# Revit family: UB90.xxx.T_RVT15
name_source: partatom
category: Möbelsysteme
revit_build: Autodesk Revit 2015 (Build: 20160512_1515(x64)
units: mm (PartAtom-declared; Revit-internal decimal feet)

## types (12) — shared parameters
1100/600 2T 2nd lvl = Nein
Beschreibung = GS-tested safety storage underbench cabinets for unrestricted storage of flammable hazardous materials in work areas in accordance with EN 14470-1 and TRGS 510 with a fire resistance of 90 (Type 90)
Cabinet & door colour = RAL 7035 Light grey
Cabinet height = 600 mm
Diff. pressure (Air change 10 times) = 1.0 Pa
Hersteller = asecos GmbH
Price information = Price from fall 2017
Price information 2 = Prices are ex works and without taxes and shipping
Product video = https://www.youtube.com
URL = https://www.asecos.com
ex. air pos. 2 = 130 mm  [stored 0.426509 ft]

## per-type parameters (varying)
- UB90.060.089.2T: 1100/500 2T 2nd lvl=Nein; 1100/500 2T perf. insert=Nein; 1100/600 2T perf. insert=Nein; 590/500 2nd lvl=Nein; 590/500 perf. insert=Nein; 590/600 2nd lvl=Nein; 590/600 perf. insert=Nein; 890/500 2T 2nd lvl=Nein; 890/500 2T perf. insert=Nein; 890/600 2T 2nd lvl=Nein; 890/600 2T perf. insert=Ja; Air change 10 times=0.6 L/s; Bestellnummer DACH=30464-001-30466; Cabinet depth=574 mm  [stored 1.8832 ft]; Cabinet width=893 mm  [stored 2.92979 ft]; Distributed load=3.07 kN/m²; Door width=416 mm; Door width RS=416 mm; Double door=Ja; Handle position=49 mm  [stored 0.160761 ft]; Kosten=1771.5 $; Modell=UB90.060.089.2T, light grey, bottom collecting sump with perforated insert; Order No. Global=30464-001-30466; Single door=Nein; Sticker HI=Nein; Sticker LO=Ja; Typenbild=30464-001.jpg; ex. air pos. 1=301 mm  [stored 0.987533 ft]
- UB90.060.059.050.T: 1100/500 2T 2nd lvl=Nein; 1100/500 2T perf. insert=Nein; 1100/600 2T perf. insert=Nein; 590/500 2nd lvl=Nein; 590/500 perf. insert=Ja; 590/600 2nd lvl=Nein; 590/600 perf. insert=Nein; 890/500 2T 2nd lvl=Nein; 890/500 2T perf. insert=Nein; 890/600 2T 2nd lvl=Nein; 890/600 2T perf. insert=Nein; Air change 10 times=0.3 L/s; Bestellnummer DACH=30483-001-30490; Cabinet depth=503 mm; Cabinet width=593 mm  [stored 1.94554 ft]; Distributed load=4.51 kN/m²; Door width=539 mm; Door width RS=495 mm; Double door=Nein; Handle position=73 mm; Kosten=1318 $; Modell=UB90.060.059.050.T, light grey, bottom collecting sump with perforated insert; Order No. Global=30483-001-30490; Single door=Ja; Sticker HI=Ja; Sticker LO=Nein; Typenbild=30483-001.jpg; ex. air pos. 1=182 mm
- UB90.060.059.T: 1100/500 2T 2nd lvl=Nein; 1100/500 2T perf. insert=Nein; 1100/600 2T perf. insert=Nein; 590/500 2nd lvl=Nein; 590/500 perf. insert=Nein; 590/600 2nd lvl=Nein; 590/600 perf. insert=Ja; 890/500 2T 2nd lvl=Nein; 890/500 2T perf. insert=Nein; 890/600 2T 2nd lvl=Nein; 890/600 2T perf. insert=Nein; Air change 10 times=0.3 L/s; Bestellnummer DACH=30481-001-30485; Cabinet depth=574 mm  [stored 1.8832 ft]; Cabinet width=593 mm  [stored 1.94554 ft]; Distributed load=4.41 kN/m²; Door width=539 mm; Door width RS=495 mm; Double door=Nein; Handle position=73 mm; Kosten=1318 $; Modell=UB90.060.059.T, light grey, bottom collecting sump with perforated insert; Order No. Global=30481-001-30485; Single door=Ja; Sticker HI=Ja; Sticker LO=Nein; Typenbild=30481-001.jpg; ex. air pos. 1=182 mm
- UB90.060.110.050.2T: 1100/500 2T 2nd lvl=Nein; 1100/500 2T perf. insert=Ja; 1100/600 2T perf. insert=Nein; 590/500 2nd lvl=Nein; 590/500 perf. insert=Nein; 590/600 2nd lvl=Nein; 590/600 perf. insert=Nein; 890/500 2T 2nd lvl=Nein; 890/500 2T perf. insert=Nein; 890/600 2T 2nd lvl=Nein; 890/600 2T perf. insert=Nein; Air change 10 times=0.6 L/s; Bestellnummer DACH=30444-001-30452; Cabinet depth=503 mm; Cabinet width=1102 mm  [stored 3.61549 ft]; Distributed load=2.73 kN/m²; Door width=521 mm  [stored 1.70932 ft]; Door width RS=521 mm  [stored 1.70932 ft]; Double door=Ja; Handle position=49 mm  [stored 0.160761 ft]; Kosten=1838.5 $; Modell=UB90.060.110.050.2T, light grey, bottom collecting sump with perforated insert; Order No. Global=30444-001-30452; Single door=Nein; Sticker HI=Ja; Sticker LO=Nein; Typenbild=30444-001.jpg; ex. air pos. 1=301 mm  [stored 0.987533 ft]
- UB90.060.089.050.2T: 1100/500 2T 2nd lvl=Nein; 1100/500 2T perf. insert=Nein; 1100/600 2T perf. insert=Nein; 590/500 2nd lvl=Nein; 590/500 perf. insert=Nein; 590/600 2nd lvl=Nein; 590/600 perf. insert=Nein; 890/500 2T 2nd lvl=Nein; 890/500 2T perf. insert=Ja; 890/600 2T 2nd lvl=Nein; 890/600 2T perf. insert=Nein; Air change 10 times=0.3 L/s; Bestellnummer DACH=30465-001-30470; Cabinet depth=503 mm; Cabinet width=893 mm  [stored 2.92979 ft]; Distributed load=3.11 kN/m²; Door width=416 mm; Door width RS=416 mm; Double door=Ja; Handle position=49 mm  [stored 0.160761 ft]; Kosten=1771.5 $; Modell=UB90.060.089.050.2T, light grey, bottom collecting sump with perforated insert; Order No. Global=30465-001-30470; Single door=Nein; Sticker HI=Nein; Sticker LO=Ja; Typenbild=30465-001.jpg; ex. air pos. 1=301 mm  [stored 0.987533 ft]
- UB90.060.110.2T: 1100/500 2T 2nd lvl=Nein; 1100/500 2T perf. insert=Nein; 1100/600 2T perf. insert=Ja; 590/500 2nd lvl=Nein; 590/500 perf. insert=Nein; 590/600 2nd lvl=Nein; 590/600 perf. insert=Nein; 890/500 2T 2nd lvl=Nein; 890/500 2T perf. insert=Nein; 890/600 2T 2nd lvl=Nein; 890/600 2T perf. insert=Nein; Air change 10 times=0.6 L/s; Bestellnummer DACH=30443-001-30447; Cabinet depth=574 mm  [stored 1.8832 ft]; Cabinet width=1102 mm  [stored 3.61549 ft]; Distributed load=2.72 kN/m²; Door width=521 mm  [stored 1.70932 ft]; Door width RS=521 mm  [stored 1.70932 ft]; Double door=Ja; Handle position=49 mm  [stored 0.160761 ft]; Kosten=1838.5 $; Modell=UB90.060.110.2T, light grey, bottom collecting sump with perforated insert; Order No. Global=30443-001-30447; Single door=Nein; Sticker HI=Ja; Sticker LO=Nein; Typenbild=30443-001.jpg; ex. air pos. 1=301 mm  [stored 0.987533 ft]
- UB90.060.059.050.T with second level shelf: 1100/500 2T 2nd lvl=Nein; 1100/500 2T perf. insert=Nein; 1100/600 2T perf. insert=Nein; 590/500 2nd lvl=Ja; 590/500 perf. insert=Ja; 590/600 2nd lvl=Nein; 590/600 perf. insert=Nein; 890/500 2T 2nd lvl=Nein; 890/500 2T perf. insert=Nein; 890/600 2T 2nd lvl=Nein; 890/600 2T perf. insert=Nein; Air change 10 times=0.3 L/s; Bestellnummer DACH=30483-001-30491; Cabinet depth=503 mm; Cabinet width=593 mm  [stored 1.94554 ft]; Distributed load=4.51 kN/m²; Door width=539 mm; Door width RS=495 mm; Double door=Nein; Handle position=73 mm; Kosten=1362 $; Modell=UB90.060.059.050.T, light grey, bottom collecting sump with perforated insert, second level shelf; Order No. Global=30483-001-30491; Single door=Ja; Sticker HI=Ja; Sticker LO=Nein; Typenbild=30483-001.jpg; ex. air pos. 1=182 mm
- UB90.060.059.T with second level shelf: 1100/500 2T 2nd lvl=Nein; 1100/500 2T perf. insert=Nein; 1100/600 2T perf. insert=Nein; 590/500 2nd lvl=Nein; 590/500 perf. insert=Nein; 590/600 2nd lvl=Ja; 590/600 perf. insert=Ja; 890/500 2T 2nd lvl=Nein; 890/500 2T perf. insert=Nein; 890/600 2T 2nd lvl=Nein; 890/600 2T perf. insert=Nein; Air change 10 times=0.3 L/s; Bestellnummer DACH=30481-001-30486; Cabinet depth=574 mm  [stored 1.8832 ft]; Cabinet width=593 mm  [stored 1.94554 ft]; Distributed load=4.41 kN/m²; Door width=539 mm; Door width RS=495 mm; Double door=Nein; Handle position=73 mm; Kosten=1348.5 $; Modell=UB90.060.059.T, light grey, bottom collecting sump with perforated insert, second level shelf; Order No. Global=30481-001-30486; Single door=Ja; Sticker HI=Ja; Sticker LO=Nein; Typenbild=30481-001.jpg; ex. air pos. 1=182 mm
- UB90.060.089.050.2T with second level shelf: 1100/500 2T 2nd lvl=Nein; 1100/500 2T perf. insert=Nein; 1100/600 2T perf. insert=Nein; 590/500 2nd lvl=Nein; 590/500 perf. insert=Nein; 590/600 2nd lvl=Nein; 590/600 perf. insert=Nein; 890/500 2T 2nd lvl=Ja; 890/500 2T perf. insert=Ja; 890/600 2T 2nd lvl=Nein; 890/600 2T perf. insert=Nein; Air change 10 times=0.3 L/s; Bestellnummer DACH=30465-001-30471; Cabinet depth=503 mm; Cabinet width=893 mm  [stored 2.92979 ft]; Distributed load=3.11 kN/m²; Door width=416 mm; Door width RS=416 mm; Double door=Ja; Handle position=49 mm  [stored 0.160761 ft]; Kosten=1827 $; Modell=UB90.060.089.050.2T, light grey, bottom collecting sump with perforated insert, second level shelf; Order No. Global=30465-001-30471; Single door=Nein; Sticker HI=Nein; Sticker LO=Ja; Typenbild=30465-001.jpg; ex. air pos. 1=301 mm  [stored 0.987533 ft]
- UB90.060.089.2T with second level shelf: 1100/500 2T 2nd lvl=Nein; 1100/500 2T perf. insert=Nein; 1100/600 2T perf. insert=Nein; 590/500 2nd lvl=Nein; 590/500 perf. insert=Nein; 590/600 2nd lvl=Nein; 590/600 perf. insert=Nein; 890/500 2T 2nd lvl=Nein; 890/500 2T perf. insert=Nein; 890/600 2T 2nd lvl=Ja; 890/600 2T perf. insert=Ja; Air change 10 times=0.6 L/s; Bestellnummer DACH=30464-001-30467; Cabinet depth=574 mm  [stored 1.8832 ft]; Cabinet width=893 mm  [stored 2.92979 ft]; Distributed load=3.07 kN/m²; Door width=416 mm; Door width RS=416 mm; Double door=Ja; Handle position=49 mm  [stored 0.160761 ft]; Kosten=1814.5 $; Modell=UB90.060.089.2T, light grey, bottom collecting sump with perforated insert, second level shelf; Order No. Global=30464-001-30467; Single door=Nein; Sticker HI=Nein; Sticker LO=Ja; Typenbild=30464-001.jpg; ex. air pos. 1=301 mm  [stored 0.987533 ft]
- UB90.060.110.050.2T with second level shelf: 1100/500 2T 2nd lvl=Ja; 1100/500 2T perf. insert=Ja; 1100/600 2T perf. insert=Nein; 590/500 2nd lvl=Nein; 590/500 perf. insert=Nein; 590/600 2nd lvl=Nein; 590/600 perf. insert=Nein; 890/500 2T 2nd lvl=Nein; 890/500 2T perf. insert=Nein; 890/600 2T 2nd lvl=Nein; 890/600 2T perf. insert=Nein; Air change 10 times=0.6 L/s; Bestellnummer DACH=30444-001-30453; Cabinet depth=503 mm; Cabinet width=1102 mm  [stored 3.61549 ft]; Distributed load=2.73 kN/m²; Door width=521 mm  [stored 1.70932 ft]; Door width RS=521 mm  [stored 1.70932 ft]; Double door=Ja; Handle position=49 mm  [stored 0.160761 ft]; Kosten=1890 $; Modell=UB90.060.110.050.2T, light grey, bottom collecting sump with perforated insert, second level shelf; Order No. Global=30444-001-30453; Single door=Nein; Sticker HI=Ja; Sticker LO=Nein; Typenbild=30444-001.jpg; ex. air pos. 1=301 mm  [stored 0.987533 ft]
- UB90.060.110.2T with second level shelf: 1100/500 2T 2nd lvl=Ja; 1100/500 2T perf. insert=Nein; 1100/600 2T perf. insert=Ja; 590/500 2nd lvl=Nein; 590/500 perf. insert=Nein; 590/600 2nd lvl=Nein; 590/600 perf. insert=Nein; 890/500 2T 2nd lvl=Nein; 890/500 2T perf. insert=Nein; 890/600 2T 2nd lvl=Nein; 890/600 2T perf. insert=Nein; Air change 10 times=0.6 L/s; Bestellnummer DACH=30443-001-30448; Cabinet depth=574 mm  [stored 1.8832 ft]; Cabinet width=1102 mm  [stored 3.61549 ft]; Distributed load=2.72 kN/m²; Door width=521 mm  [stored 1.70932 ft]; Door width RS=521 mm  [stored 1.70932 ft]; Double door=Ja; Handle position=49 mm  [stored 0.160761 ft]; Kosten=1876.5 $; Modell=UB90.060.110.2T, light grey, bottom collecting sump with perforated insert, second level shelf; Order No. Global=30443-001-30448; Single door=Nein; Sticker HI=Ja; Sticker LO=Nein; Typenbild=30443-001.jpg; ex. air pos. 1=301 mm  [stored 0.987533 ft]

note: [stored X ft] marks values corroborated as IEEE doubles in the binary element streams (Revit-internal decimal feet)
